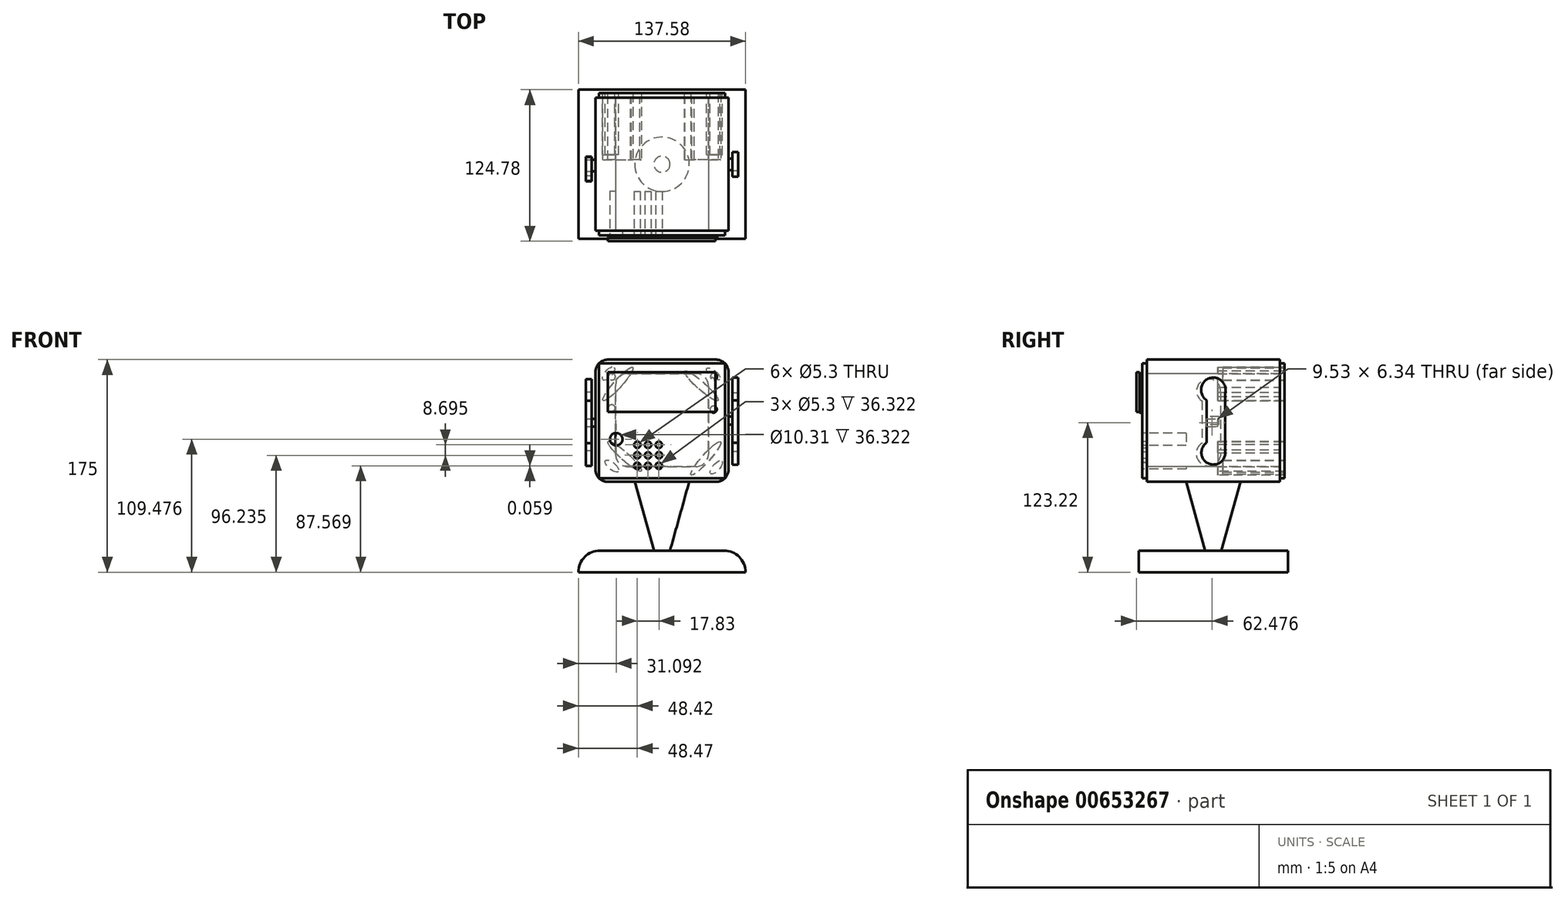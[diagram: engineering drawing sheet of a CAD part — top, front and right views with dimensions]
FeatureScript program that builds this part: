
annotation { "Feature Type Name" : "Feature", "Feature Type Description" : "" }
export const myFeature = defineFeature(function(context is Context, id is Id, definition is map)
    precondition{}
    {
        {
            var Q0;
            Q0=qCreatedBy(makeId("Top.planeOp"),FACE);
            var sketch = newSketch(context, id + "F0", { "sketchPlane" : qUnion([Q0])});
            skCircle(sketch, "E0.cCircle", {"center": v(0, 0) * mm, "radius": 54.77 * mm, "construction": true});
            skLineSegment(sketch, "E0.0", {"start": v(54.77, -54.77) * mm, "end": v(-54.77, -54.77) * mm});
            skLineSegment(sketch, "E0.1", {"start": v(-54.77, -54.77) * mm, "end": v(-54.77, 54.77) * mm});
            skLineSegment(sketch, "E0.2", {"start": v(-54.77, 54.77) * mm, "end": v(54.77, 54.77) * mm});
            skLineSegment(sketch, "E0.3", {"start": v(54.77, 54.77) * mm, "end": v(54.77, -54.77) * mm});
            skPoint(sketch, "E0.0.midPoint", {"position": v(0, -54.77) * mm});
            skSolve(sketch);
        }
        {
            var Q0;
            Q0 = qSketchRegion(id + "F0", true);
            extrude(context, id + "F1", {"entities" : qUnion([Q0]), "depth" : 100.58 * mm, "offsetDistance" : 25.4 * mm});
        }
        {
            var Q0;
            Q0=makeQuery(id+"F1.opExtrude","CAP_EDGE",EDGE,{"disambiguationData":[OSD([sQuery(id+"F0.wireOp",EDGE,"E0.1")])],"isStart":false});
            var Q1;
            Q1=makeQuery(id+"F1.opExtrude","CAP_EDGE",EDGE,{"disambiguationData":[OSD([sQuery(id+"F0.wireOp",EDGE,"E0.3")])],"isStart":false});
            var Q2;
            Q2=makeQuery(id+"F1.opExtrude","CAP_EDGE",EDGE,{"disambiguationData":[OSD([sQuery(id+"F0.wireOp",EDGE,"E0.3")])],"isStart":true});
            var Q3;
            Q3=makeQuery(id+"F1.opExtrude","CAP_EDGE",EDGE,{"disambiguationData":[OSD([sQuery(id+"F0.wireOp",EDGE,"E0.1")])],"isStart":true});
            fillet(context, id + "F2", {"entities" : qUnion([Q0, Q1, Q2, Q3]), "radius" : 10.16 * mm, "tangentPropagation" : true, "allowEdgeOverflow" : false});
        }
        {
            var Q0;
            Q0=makeQuery(id+"F1.opExtrude","SWEPT_FACE",FACE,{"disambiguationData":[OSD([sQuery(id+"F0.wireOp",EDGE,"E0.0")])]});
            var sketch = newSketch(context, id + "F3", { "sketchPlane" : qUnion([Q0])});
            skPoint(sketch, "E1", {"position": v(0, 50.3) * mm});
            skPoint(sketch, "E1.positionSnap0", {"position": v(-54.77, 50.3) * mm});
            skSolve(sketch);
        }
        {
            var Q0;
            {var subQ0=sQuery(id+"F0.wireOp",EDGE,"E0.0");Q0=makeQuery(id+"F3.imprint","IMPRINT",FACE,{"disambiguationData":[TD([[makeQuery(id+"F3.imprint","IMPRINT",EDGE,{"derivedFrom":makeQuery(id+"F1.opExtrude","CAP_EDGE",EDGE,{"disambiguationData":[OSD([subQ0])],"isStart":true})}),-1.0]])]});}
            var sketch = newSketch(context, id + "F4", { "sketchPlane" : qUnion([Q0])});
            skLineSegment(sketch, "E2.0", {"start": v(38.27, 12.57) * mm, "end": v(-38.27, 12.57) * mm});
            skLineSegment(sketch, "E2.1", {"start": v(-38.27, 12.57) * mm, "end": v(-38.27, 89.12) * mm});
            skLineSegment(sketch, "E2.2", {"start": v(-38.27, 89.12) * mm, "end": v(38.27, 89.12) * mm});
            skLineSegment(sketch, "E2.3", {"start": v(38.27, 89.12) * mm, "end": v(38.27, 12.57) * mm});
            skPoint(sketch, "E2.0.midPoint", {"position": v(0, 12.57) * mm});
            skSolve(sketch);
        }
        {
            var Q0;
            Q0=makeQuery(id+"F4.imprint","IMPRINT",FACE,{"disambiguationData":[TD([[makeQuery(id+"F4.imprint","IMPRINT",EDGE,{"derivedFrom":sQuery(id+"F4.wireOp",EDGE,"E2.0")}),-1.0]])]});
            extrude(context, id + "F5", {"entities" : qUnion([Q0]), "operationType" : NewBodyOperationType.REMOVE, "oppositeDirection" : true, "depth" : 148.34 * mm, "offsetDistance" : 25.4 * mm});
        }
        {
            var Q0;
            Q0=makeQuery(id+"F5.boolean.opBoolean","COPY",EDGE,{"derivedFrom":makeQuery(id+"F5.opExtrude","SWEPT_EDGE",EDGE,{"disambiguationData":[OSD([sQuery(id+"F4.wireOp",EDGE,"E2.0"),sQuery(id+"F4.wireOp",EDGE,"E2.1")])]})});
            var Q1;
            Q1=makeQuery(id+"F5.boolean.opBoolean","COPY",EDGE,{"derivedFrom":makeQuery(id+"F5.opExtrude","SWEPT_EDGE",EDGE,{"disambiguationData":[OSD([sQuery(id+"F4.wireOp",EDGE,"E2.2"),sQuery(id+"F4.wireOp",EDGE,"E2.3")])]})});
            var Q2;
            Q2=makeQuery(id+"F5.boolean.opBoolean","COPY",EDGE,{"derivedFrom":makeQuery(id+"F5.opExtrude","SWEPT_EDGE",EDGE,{"disambiguationData":[OSD([sQuery(id+"F4.wireOp",EDGE,"E2.0"),sQuery(id+"F4.wireOp",EDGE,"E2.3")])]})});
            var Q3;
            Q3=makeQuery(id+"F5.boolean.opBoolean","COPY",EDGE,{"derivedFrom":makeQuery(id+"F5.opExtrude","SWEPT_EDGE",EDGE,{"disambiguationData":[OSD([sQuery(id+"F4.wireOp",EDGE,"E2.1"),sQuery(id+"F4.wireOp",EDGE,"E2.2")])]})});
            fillet(context, id + "F6", {"entities" : qUnion([Q0, Q1, Q2, Q3]), "radius" : 10.16 * mm, "tangentPropagation" : true, "allowEdgeOverflow" : false});
        }
        {
            var Q0;
            Q0=makeQuery(id+"F1.opExtrude","SWEPT_FACE",FACE,{"disambiguationData":[OSD([sQuery(id+"F0.wireOp",EDGE,"E0.0")])]});
            var sketch = newSketch(context, id + "F7", { "sketchPlane" : qUnion([Q0])});
            skLineSegment(sketch, "E3.bottom", {"start": v(-51.8, 97.6) * mm, "end": v(51.8, 97.6) * mm});
            skLineSegment(sketch, "E3.top", {"start": v(-51.8, 2.98) * mm, "end": v(51.8, 2.98) * mm});
            skLineSegment(sketch, "E3.left", {"start": v(-51.8, 97.6) * mm, "end": v(-51.8, 2.98) * mm});
            skLineSegment(sketch, "E3.right", {"start": v(51.8, 97.6) * mm, "end": v(51.8, 2.98) * mm});
            skSolve(sketch);
        }
        {
            var Q0;
            Q0 = qSketchRegion(id + "F7", true);
            extrude(context, id + "F8", {"entities" : qUnion([Q0]), "operationType" : NewBodyOperationType.ADD, "depth" : 3.8 * mm, "offsetDistance" : 25.4 * mm});
        }
        {
            var Q0;
            Q0=makeQuery(id+"F1.opExtrude","CAP_FACE",FACE,{"disambiguationData":[OSD([sQuery(id+"F0.wireOp",EDGE,"E0.0"),sQuery(id+"F0.wireOp",EDGE,"E0.1"),sQuery(id+"F0.wireOp",EDGE,"E0.2"),sQuery(id+"F0.wireOp",EDGE,"E0.3")])],"isStart":true});
            var sketch = newSketch(context, id + "F9", { "sketchPlane" : qUnion([Q0])});
            skCircle(sketch, "E4", {"center": v(0, 0) * mm, "radius": 22.39 * mm});
            skSolve(sketch);
        }
        {
            var Q0;
            Q0=qCreatedBy(makeId("Top.planeOp"),FACE);
            cPlane(context, id + "F10", {"entities" : qUnion([Q0]), "cplaneType" : CPlaneType.OFFSET, "offset" : 56.64 * mm, "oppositeDirection" : true, "width" : 152.4 * mm, "height" : 152.4 * mm});
        }
        {
            var Q0;
            Q0=qCreatedBy(id+"F10.planeOp",FACE);
            var sketch = newSketch(context, id + "F11", { "sketchPlane" : qUnion([Q0])});
            skCircle(sketch, "E5", {"center": v(0, 0) * mm, "radius": 6.62 * mm});
            skSolve(sketch);
        }
        {
            var Q1;
            Q1=makeQuery(id+"F9.imprint","IMPRINT",FACE,{"disambiguationData":[TD([[makeQuery(id+"F9.imprint","IMPRINT",EDGE,{"derivedFrom":sQuery(id+"F9.wireOp",EDGE,"E4")}),1.0]])]});
            var Q2;
            Q2=makeQuery(id+"F11.imprint","IMPRINT",FACE,{"disambiguationData":[TD([[makeQuery(id+"F11.imprint","IMPRINT",EDGE,{"derivedFrom":sQuery(id+"F11.wireOp",EDGE,"E5")}),1.0]])]});
            loft(context, id + "F12", {"operationType" : NewBodyOperationType.ADD, "sheetProfilesArray" : [{ "sheetProfileEntities" : qUnion([Q1]) }, { "sheetProfileEntities" : qUnion([Q2]) }]});
        }
        {
            var Q0;
            Q0=qCreatedBy(id+"F10.planeOp",FACE);
            cPlane(context, id + "F13", {"entities" : qUnion([Q0]), "cplaneType" : CPlaneType.OFFSET, "offset" : 17.78 * mm, "oppositeDirection" : true, "width" : 152.4 * mm, "height" : 152.4 * mm});
        }
        {
            var Q0;
            Q0=qCreatedBy(id+"F13.planeOp",FACE);
            var sketch = newSketch(context, id + "F14", { "sketchPlane" : qUnion([Q0])});
            skLineSegment(sketch, "E6.bottom", {"start": v(68.8, -61.37) * mm, "end": v(-68.8, -61.37) * mm});
            skLineSegment(sketch, "E6.top", {"start": v(68.8, 61.37) * mm, "end": v(-68.8, 61.37) * mm});
            skLineSegment(sketch, "E6.left", {"start": v(68.8, -61.37) * mm, "end": v(68.8, 61.37) * mm});
            skLineSegment(sketch, "E6.right", {"start": v(-68.8, -61.37) * mm, "end": v(-68.8, 61.37) * mm});
            skPoint(sketch, "E6.middle", {"position": v(0, 0) * mm});
            skSolve(sketch);
        }
        {
            var Q0;
            Q0=makeQuery(id+"F14.imprint","IMPRINT",FACE,{"disambiguationData":[TD([[makeQuery(id+"F14.imprint","IMPRINT",EDGE,{"derivedFrom":sQuery(id+"F14.wireOp",EDGE,"E6.bottom")}),-1.0]])]});
            extrude(context, id + "F15", {"entities" : qUnion([Q0]), "operationType" : NewBodyOperationType.ADD, "depth" : 17.78 * mm, "offsetDistance" : 25.4 * mm});
        }
        {
            var Q0;
            Q0=makeQuery(id+"F15.opExtrude","CAP_EDGE",EDGE,{"disambiguationData":[OSD([sQuery(id+"F14.wireOp",EDGE,"E6.left")])],"isStart":false});
            var Q1;
            Q1=makeQuery(id+"F15.opExtrude","CAP_EDGE",EDGE,{"disambiguationData":[OSD([sQuery(id+"F14.wireOp",EDGE,"E6.right")])],"isStart":false});
            fillet(context, id + "F16", {"entities" : qUnion([Q0, Q1]), "radius" : 17.78 * mm, "tangentPropagation" : true, "allowEdgeOverflow" : false});
        }
        {
            var Q0;
            Q0=makeQuery(id+"F1.opExtrude","SWEPT_FACE",FACE,{"disambiguationData":[OSD([sQuery(id+"F0.wireOp",EDGE,"E0.2")])]});
            var sketch = newSketch(context, id + "F17", { "sketchPlane" : qUnion([Q0])});
            skLineSegment(sketch, "E7.bottom", {"start": v(-51.8, 97.6) * mm, "end": v(51.8, 97.6) * mm});
            skLineSegment(sketch, "E7.top", {"start": v(-51.8, 2.98) * mm, "end": v(51.8, 2.98) * mm});
            skLineSegment(sketch, "E7.left", {"start": v(-51.8, 97.6) * mm, "end": v(-51.8, 2.98) * mm});
            skLineSegment(sketch, "E7.right", {"start": v(51.8, 97.6) * mm, "end": v(51.8, 2.98) * mm});
            skSolve(sketch);
        }
        {
            var Q0;
            Q0 = qSketchRegion(id + "F17", true);
            extrude(context, id + "F18", {"entities" : qUnion([Q0]), "operationType" : NewBodyOperationType.ADD, "depth" : 3.8 * mm, "offsetDistance" : 25.4 * mm});
        }
        {
            var Q0;
            Q0=makeQuery(id+"F18.opExtrude","CAP_FACE",FACE,{"disambiguationData":[OSD([sQuery(id+"F17.wireOp",EDGE,"E7.bottom"),sQuery(id+"F17.wireOp",EDGE,"E7.top"),sQuery(id+"F17.wireOp",EDGE,"E7.left"),sQuery(id+"F17.wireOp",EDGE,"E7.right")])],"isStart":false});
            var sketch = newSketch(context, id + "F19", { "sketchPlane" : qUnion([Q0])});
            skEllipse(sketch, "E8", {"center": v(-42.25, 88.86) * mm, "majorRadius": 6.99 * mm, "minorRadius": 2.87 * mm, "majorAxis": v(-0.76, -0.65)});
            skEllipse(sketch, "E9.1.0.0", {"center": v(41.15, 12.95) * mm, "majorRadius": 6.99 * mm, "minorRadius": 2.87 * mm, "majorAxis": v(-0.76, -0.65)});
            skEllipse(sketch, "E9.2.0.0", {"center": v(124.54, -62.95) * mm, "majorRadius": 6.99 * mm, "minorRadius": 2.87 * mm, "majorAxis": v(-0.76, -0.65)});
            skEllipse(sketch, "E10", {"center": v(44.02, 89.18) * mm, "majorRadius": 6.99 * mm, "minorRadius": 2.87 * mm, "majorAxis": v(-0.65, 0.76)});
            skEllipse(sketch, "E11.1.0.0", {"center": v(-44.7, 11.94) * mm, "majorRadius": 6.99 * mm, "minorRadius": 2.87 * mm, "majorAxis": v(-0.65, 0.76)});
            skSolve(sketch);
        }
        {
            var Q0;
            Q0=makeQuery(id+"F19.imprint","IMPRINT",FACE,{"disambiguationData":[TD([[makeQuery(id+"F19.imprint","IMPRINT",EDGE,{"derivedFrom":sQuery(id+"F19.wireOp",EDGE,"E8")}),1.0]])]});
            var Q1;
            Q1=makeQuery(id+"F19.imprint","IMPRINT",FACE,{"disambiguationData":[TD([[makeQuery(id+"F19.imprint","IMPRINT",EDGE,{"derivedFrom":sQuery(id+"F19.wireOp",EDGE,"E10")}),1.0]])]});
            var Q2;
            Q2=makeQuery(id+"F19.imprint","IMPRINT",FACE,{"disambiguationData":[TD([[makeQuery(id+"F19.imprint","IMPRINT",EDGE,{"derivedFrom":sQuery(id+"F19.wireOp",EDGE,"E9.1.0.0")}),1.0]])]});
            var Q3;
            Q3=makeQuery(id+"F19.imprint","IMPRINT",FACE,{"disambiguationData":[TD([[makeQuery(id+"F19.imprint","IMPRINT",EDGE,{"derivedFrom":sQuery(id+"F19.wireOp",EDGE,"E11.1.0.0")}),1.0]])]});
            extrude(context, id + "F20", {"entities" : qUnion([Q0, Q1, Q2, Q3]), "operationType" : NewBodyOperationType.REMOVE, "oppositeDirection" : true, "depth" : 50.8 * mm, "offsetDistance" : 25.4 * mm});
        }
        {
            var Q0;
            Q0=makeQuery(id+"F18.opExtrude","CAP_FACE",FACE,{"disambiguationData":[OSD([sQuery(id+"F17.wireOp",EDGE,"E7.bottom"),sQuery(id+"F17.wireOp",EDGE,"E7.top"),sQuery(id+"F17.wireOp",EDGE,"E7.left"),sQuery(id+"F17.wireOp",EDGE,"E7.right")])],"isStart":false});
            var sketch = newSketch(context, id + "F21", { "sketchPlane" : qUnion([Q0])});
            skEllipse(sketch, "E12", {"center": v(-32.4, 79) * mm, "majorRadius": 18.25 * mm, "minorRadius": 3.26 * mm, "majorAxis": v(-0.75, -0.66)});
            skEllipse(sketch, "E13.1.0.0", {"center": v(30.73, 21.08) * mm, "majorRadius": 18.25 * mm, "minorRadius": 3.26 * mm, "majorAxis": v(-0.75, -0.66)});
            skEllipse(sketch, "E14", {"center": v(36.25, 80.6) * mm, "majorRadius": 18.25 * mm, "minorRadius": 3.26 * mm, "majorAxis": v(-0.66, 0.75)});
            skEllipse(sketch, "E15.1.0.0", {"center": v(-36.07, 19.3) * mm, "majorRadius": 18.25 * mm, "minorRadius": 3.26 * mm, "majorAxis": v(-0.66, 0.75)});
            skSolve(sketch);
        }
        {
            var Q0;
            Q0=makeQuery(id+"F21.imprint","IMPRINT",FACE,{"disambiguationData":[TD([[makeQuery(id+"F21.imprint","IMPRINT",EDGE,{"derivedFrom":sQuery(id+"F21.wireOp",EDGE,"E12")}),1.0]])]});
            var Q1;
            Q1=makeQuery(id+"F21.imprint","IMPRINT",FACE,{"disambiguationData":[TD([[makeQuery(id+"F21.imprint","IMPRINT",EDGE,{"derivedFrom":sQuery(id+"F21.wireOp",EDGE,"E13.1.0.0")}),1.0]])]});
            var Q2;
            Q2=makeQuery(id+"F21.imprint","IMPRINT",FACE,{"disambiguationData":[TD([[makeQuery(id+"F21.imprint","IMPRINT",EDGE,{"derivedFrom":sQuery(id+"F21.wireOp",EDGE,"E15.1.0.0")}),1.0]])]});
            var Q3;
            Q3=makeQuery(id+"F21.imprint","IMPRINT",FACE,{"disambiguationData":[TD([[makeQuery(id+"F21.imprint","IMPRINT",EDGE,{"derivedFrom":sQuery(id+"F21.wireOp",EDGE,"E14")}),1.0]])]});
            extrude(context, id + "F22", {"entities" : qUnion([Q0, Q1, Q2, Q3]), "operationType" : NewBodyOperationType.REMOVE, "oppositeDirection" : true, "depth" : 54.86 * mm, "offsetDistance" : 25.4 * mm});
        }
        {
            var Q0;
            Q0=makeQuery(id+"F8.opExtrude","CAP_FACE",FACE,{"disambiguationData":[OSD([sQuery(id+"F7.wireOp",EDGE,"E3.bottom"),sQuery(id+"F7.wireOp",EDGE,"E3.top"),sQuery(id+"F7.wireOp",EDGE,"E3.left"),sQuery(id+"F7.wireOp",EDGE,"E3.right")])],"isStart":false});
            var sketch = newSketch(context, id + "F23", { "sketchPlane" : qUnion([Q0])});
            skCircle(sketch, "E16", {"center": v(-41.1, 86.58) * mm, "radius": 2.76 * mm});
            skCircle(sketch, "E17.1.0.0", {"center": v(42.67, 86.61) * mm, "radius": 2.76 * mm});
            skCircle(sketch, "E18.1.0.0", {"center": v(-41.4, 60.7) * mm, "radius": 2.76 * mm});
            skCircle(sketch, "E19.1.0.0", {"center": v(42.42, 59.7) * mm, "radius": 2.76 * mm});
            skSolve(sketch);
        }
        {
            var Q0;
            Q0=makeQuery(id+"F23.imprint","IMPRINT",FACE,{"disambiguationData":[TD([[makeQuery(id+"F23.imprint","IMPRINT",EDGE,{"derivedFrom":sQuery(id+"F23.wireOp",EDGE,"E17.2.0.0")}),1.0]])]});
            var Q1;
            Q1=makeQuery(id+"F23.imprint","IMPRINT",FACE,{"disambiguationData":[TD([[makeQuery(id+"F23.imprint","IMPRINT",EDGE,{"derivedFrom":sQuery(id+"F23.wireOp",EDGE,"E16")}),1.0]])]});
            var Q2;
            Q2=makeQuery(id+"F23.imprint","IMPRINT",FACE,{"disambiguationData":[TD([[makeQuery(id+"F23.imprint","IMPRINT",EDGE,{"derivedFrom":sQuery(id+"F23.wireOp",EDGE,"E18.1.0.0")}),1.0]])]});
            var Q3;
            Q3=makeQuery(id+"F23.imprint","IMPRINT",FACE,{"disambiguationData":[TD([[makeQuery(id+"F23.imprint","IMPRINT",EDGE,{"derivedFrom":sQuery(id+"F23.wireOp",EDGE,"E17.1.0.0")}),1.0]])]});
            var Q4;
            Q4=makeQuery(id+"F23.imprint","IMPRINT",FACE,{"disambiguationData":[TD([[makeQuery(id+"F23.imprint","IMPRINT",EDGE,{"derivedFrom":sQuery(id+"F23.wireOp",EDGE,"E19.1.0.0")}),1.0]])]});
            extrude(context, id + "F24", {"entities" : qUnion([Q0, Q1, Q2, Q3, Q4]), "operationType" : NewBodyOperationType.ADD, "depth" : 2.03 * mm, "offsetDistance" : 25.4 * mm});
        }
        {
            var Q0;
            Q0=makeQuery(id+"F24.opExtrude","CAP_FACE",FACE,{"disambiguationData":[OSD([sQuery(id+"F23.wireOp",EDGE,"E19.1.0.0")])],"isStart":false});
            var sketch = newSketch(context, id + "F25", { "sketchPlane" : qUnion([Q0])});
            skLineSegment(sketch, "E20.bottom", {"start": v(-44.52, 90.37) * mm, "end": v(43.99, 90.37) * mm});
            skLineSegment(sketch, "E20.top", {"start": v(-44.52, 57.42) * mm, "end": v(43.99, 57.42) * mm});
            skLineSegment(sketch, "E20.left", {"start": v(-44.52, 90.37) * mm, "end": v(-44.52, 57.42) * mm});
            skLineSegment(sketch, "E20.right", {"start": v(43.99, 90.37) * mm, "end": v(43.99, 57.42) * mm});
            skSolve(sketch);
        }
        {
            var Q0;
            Q0 = qSketchRegion(id + "F25", true);
            extrude(context, id + "F26", {"entities" : qUnion([Q0]), "operationType" : NewBodyOperationType.ADD, "depth" : 2.8 * mm, "offsetDistance" : 25.4 * mm});
        }
        {
            var Q0;
            Q0=makeQuery(id+"F8.opExtrude","CAP_FACE",FACE,{"disambiguationData":[OSD([sQuery(id+"F7.wireOp",EDGE,"E3.bottom"),sQuery(id+"F7.wireOp",EDGE,"E3.top"),sQuery(id+"F7.wireOp",EDGE,"E3.left"),sQuery(id+"F7.wireOp",EDGE,"E3.right")])],"isStart":false});
            var sketch = newSketch(context, id + "F27", { "sketchPlane" : qUnion([Q0])});
            skCircle(sketch, "E21", {"center": v(-37.7, 35.06) * mm, "radius": 5.15 * mm});
            skCircle(sketch, "E22", {"center": v(-20.27, 30.5) * mm, "radius": 2.65 * mm});
            skCircle(sketch, "E23.1.0.0", {"center": v(-11.43, 30.48) * mm, "radius": 2.65 * mm});
            skCircle(sketch, "E23.2.0.0", {"center": v(-2.59, 30.45) * mm, "radius": 2.65 * mm});
            skCircle(sketch, "E24.1.0.0", {"center": v(-20.32, 21.84) * mm, "radius": 2.65 * mm});
            skCircle(sketch, "E24.1.0.1", {"center": v(-11.48, 21.81) * mm, "radius": 2.65 * mm});
            skCircle(sketch, "E24.2.0.0", {"center": v(-20.37, 13.18) * mm, "radius": 2.65 * mm});
            skCircle(sketch, "E24.2.0.1", {"center": v(-11.53, 13.15) * mm, "radius": 2.65 * mm});
            skCircle(sketch, "E25.1.0.0", {"center": v(-2.54, 13.2) * mm, "radius": 2.65 * mm});
            skCircle(sketch, "E25.1.0.1", {"center": v(-2.5, 21.87) * mm, "radius": 2.65 * mm});
            skSolve(sketch);
        }
        {
            var Q0;
            Q0=makeQuery(id+"F27.imprint","IMPRINT",FACE,{"disambiguationData":[TD([[makeQuery(id+"F27.imprint","IMPRINT",EDGE,{"derivedFrom":sQuery(id+"F27.wireOp",EDGE,"E21")}),1.0]])]});
            var Q1;
            Q1=makeQuery(id+"F27.imprint","IMPRINT",FACE,{"disambiguationData":[TD([[makeQuery(id+"F27.imprint","IMPRINT",EDGE,{"derivedFrom":sQuery(id+"F27.wireOp",EDGE,"E22")}),1.0]])]});
            var Q2;
            Q2=makeQuery(id+"F27.imprint","IMPRINT",FACE,{"disambiguationData":[TD([[makeQuery(id+"F27.imprint","IMPRINT",EDGE,{"derivedFrom":sQuery(id+"F27.wireOp",EDGE,"E23.1.0.0")}),1.0]])]});
            var Q3;
            Q3=makeQuery(id+"F27.imprint","IMPRINT",FACE,{"disambiguationData":[TD([[makeQuery(id+"F27.imprint","IMPRINT",EDGE,{"derivedFrom":sQuery(id+"F27.wireOp",EDGE,"E23.2.0.0")}),1.0]])]});
            var Q4;
            Q4=makeQuery(id+"F27.imprint","IMPRINT",FACE,{"disambiguationData":[TD([[makeQuery(id+"F27.imprint","IMPRINT",EDGE,{"derivedFrom":sQuery(id+"F27.wireOp",EDGE,"E25.1.0.1")}),1.0]])]});
            var Q5;
            Q5=makeQuery(id+"F27.imprint","IMPRINT",FACE,{"disambiguationData":[TD([[makeQuery(id+"F27.imprint","IMPRINT",EDGE,{"derivedFrom":sQuery(id+"F27.wireOp",EDGE,"E24.1.0.1")}),1.0]])]});
            var Q6;
            Q6=makeQuery(id+"F27.imprint","IMPRINT",FACE,{"disambiguationData":[TD([[makeQuery(id+"F27.imprint","IMPRINT",EDGE,{"derivedFrom":sQuery(id+"F27.wireOp",EDGE,"E24.1.0.0")}),1.0]])]});
            var Q7;
            Q7=makeQuery(id+"F27.imprint","IMPRINT",FACE,{"disambiguationData":[TD([[makeQuery(id+"F27.imprint","IMPRINT",EDGE,{"derivedFrom":sQuery(id+"F27.wireOp",EDGE,"E24.2.0.0")}),1.0]])]});
            var Q8;
            Q8=makeQuery(id+"F27.imprint","IMPRINT",FACE,{"disambiguationData":[TD([[makeQuery(id+"F27.imprint","IMPRINT",EDGE,{"derivedFrom":sQuery(id+"F27.wireOp",EDGE,"E24.2.0.1")}),1.0]])]});
            var Q9;
            Q9=makeQuery(id+"F27.imprint","IMPRINT",FACE,{"disambiguationData":[TD([[makeQuery(id+"F27.imprint","IMPRINT",EDGE,{"derivedFrom":sQuery(id+"F27.wireOp",EDGE,"E25.1.0.0")}),1.0]])]});
            var Q10;
            Q10=sQuery(id+"F27.wireOp",EDGE,"E21");
            extrude(context, id + "F28", {"entities" : qUnion([Q0, Q1, Q2, Q3, Q4, Q5, Q6, Q7, Q8, Q9]), "operationType" : NewBodyOperationType.REMOVE, "surfaceEntities" : qUnion([Q10]), "oppositeDirection" : true, "depth" : 36.32 * mm, "offsetDistance" : 25.4 * mm});
        }
        {
            var Q0;
            Q0=makeQuery(id+"F1.opExtrude","SWEPT_FACE",FACE,{"disambiguationData":[OSD([sQuery(id+"F0.wireOp",EDGE,"E0.3")])]});
            var sketch = newSketch(context, id + "F29", { "sketchPlane" : qUnion([Q0])});
            skLineSegment(sketch, "E26.bottom", {"start": v(4.77, 46.96) * mm, "end": v(-4.77, 46.96) * mm});
            skLineSegment(sketch, "E26.top", {"start": v(4.77, 53.63) * mm, "end": v(-4.77, 53.63) * mm});
            skLineSegment(sketch, "E26.left", {"start": v(4.77, 46.96) * mm, "end": v(4.77, 53.63) * mm});
            skLineSegment(sketch, "E26.right", {"start": v(-4.77, 46.96) * mm, "end": v(-4.77, 53.63) * mm});
            skPoint(sketch, "E26.middle", {"position": v(0, 50.3) * mm});
            skPoint(sketch, "E26.middle.positionSnap0", {"position": v(0, 10.16) * mm});
            skPoint(sketch, "E26.middle.positionSnap1", {"position": v(-54.77, 50.3) * mm});
            skPoint(sketch, "E26.centerSnap0", {"position": v(0, 10.16) * mm});
            skPoint(sketch, "E26.centerSnap1", {"position": v(-54.77, 50.3) * mm});
            skSolve(sketch);
        }
        {
            var Q0;
            Q0 = qSketchRegion(id + "F29", true);
            extrude(context, id + "F30", {"entities" : qUnion([Q0]), "operationType" : NewBodyOperationType.ADD, "depth" : 3.05 * mm, "offsetDistance" : 25.4 * mm});
        }
        {
            var Q0;
            Q0=makeQuery(id+"F30.opExtrude","CAP_FACE",FACE,{"disambiguationData":[OSD([sQuery(id+"F29.wireOp",EDGE,"E26.bottom"),sQuery(id+"F29.wireOp",EDGE,"E26.top"),sQuery(id+"F29.wireOp",EDGE,"E26.left"),sQuery(id+"F29.wireOp",EDGE,"E26.right")])],"isStart":false});
            var sketch = newSketch(context, id + "F31", { "sketchPlane" : qUnion([Q0])});
            skCircle(sketch, "E27", {"center": v(0, 75.69) * mm, "radius": 10.1 * mm});
            skPoint(sketch, "E27.centerSnap0", {"position": v(0, 53.63) * mm});
            skCircle(sketch, "E28", {"center": v(0, 24.03) * mm, "radius": 9.84 * mm});
            skPoint(sketch, "E28.centerSnap0", {"position": v(0, 46.96) * mm});
            skLineSegment(sketch, "E29", {"start": v(9.81, 24.74) * mm, "end": v(9.81, 73.25) * mm});
            skLineSegment(sketch, "E30", {"start": v(-5.45, 32.22) * mm, "end": v(-5.45, 67.17) * mm});
            skSolve(sketch);
        }
        {
            var Q0;
            Q0 = qSketchRegion(id + "F31", true);
            extrude(context, id + "F32", {"entities" : qUnion([Q0]), "depth" : 4.83 * mm, "offsetDistance" : 25.4 * mm});
        }
        {
            var Q0;
            Q0=makeQuery(id+"F1.opExtrude","SWEPT_FACE",FACE,{"disambiguationData":[OSD([sQuery(id+"F0.wireOp",EDGE,"E0.1")])]});
            var sketch = newSketch(context, id + "F33", { "sketchPlane" : qUnion([Q0])});
            skLineSegment(sketch, "E31.bottom", {"start": v(5.7, 45.63) * mm, "end": v(-3.83, 45.63) * mm});
            skLineSegment(sketch, "E31.top", {"start": v(5.7, 51.97) * mm, "end": v(-3.83, 51.97) * mm});
            skLineSegment(sketch, "E31.left", {"start": v(5.7, 45.63) * mm, "end": v(5.7, 51.97) * mm});
            skLineSegment(sketch, "E31.right", {"start": v(-3.83, 45.63) * mm, "end": v(-3.83, 51.97) * mm});
            skSolve(sketch);
        }
        {
            var Q0;
            Q0 = qSketchRegion(id + "F33", true);
            extrude(context, id + "F34", {"entities" : qUnion([Q0]), "operationType" : NewBodyOperationType.ADD, "depth" : 3.05 * mm, "offsetDistance" : 25.4 * mm});
        }
        {
            var Q0;
            Q0=makeQuery(id+"F34.opExtrude","CAP_FACE",FACE,{"disambiguationData":[OSD([sQuery(id+"F33.wireOp",EDGE,"E31.bottom"),sQuery(id+"F33.wireOp",EDGE,"E31.top"),sQuery(id+"F33.wireOp",EDGE,"E31.left"),sQuery(id+"F33.wireOp",EDGE,"E31.right")])],"isStart":false});
            var sketch = newSketch(context, id + "F35", { "sketchPlane" : qUnion([Q0])});
            skCircle(sketch, "E32.2.0", {"center": v(3.91, 23.18) * mm, "radius": 10.1 * mm});
            skLineSegment(sketch, "E32.2.1", {"start": v(-5.9, 74.16) * mm, "end": v(-5.9, 25.65) * mm});
            skLineSegment(sketch, "E32.2.2", {"start": v(9.36, 66.67) * mm, "end": v(9.36, 31.7) * mm});
            skCircle(sketch, "E32.2.3", {"center": v(3.92, 74.86) * mm, "radius": 9.84 * mm});
            skSolve(sketch);
        }
        {
            var Q0;
            {var subQ1=sQuery(id+"F35.wireOp",EDGE,"E32.2.1");Q0=makeQuery(id+"F35.imprint","IMPRINT",FACE,{"disambiguationData":[TD([[makeQuery(id+"F35.imprint","IMPRINT",EDGE,{"derivedFrom":subQ1}),1.0]])]});}
            var Q1;
            {var subQ0=sQuery(id+"F35.wireOp",EDGE,"E32.2.3");var subQ1=makeQuery(id+"F35.imprint","INTERSECT",VERTEX,{"derivedFrom":[sQuery(id+"F35.wireOp",EDGE,"E32.2.1"),subQ0]});Q1=makeQuery(id+"F35.imprint","IMPRINT",FACE,{"disambiguationData":[TD([[makeQuery(id+"F35.imprint","IMPRINT",EDGE,{"disambiguationData":[TD([[subQ1,-1.0]])],"derivedFrom":subQ0}),1.0]])]});}
            var Q2;
            {var subQ0=sQuery(id+"F35.wireOp",EDGE,"E32.2.0");var subQ1=makeQuery(id+"F35.imprint","INTERSECT",VERTEX,{"derivedFrom":[subQ0,sQuery(id+"F35.wireOp",EDGE,"E32.2.1")]});Q2=makeQuery(id+"F35.imprint","IMPRINT",FACE,{"disambiguationData":[TD([[makeQuery(id+"F35.imprint","IMPRINT",EDGE,{"disambiguationData":[TD([[subQ1,1.0]])],"derivedFrom":subQ0}),1.0]])]});}
            var Q3;
            Q3=sQuery(id+"F35.wireOp",EDGE,"E32.2.3");
            var Q4;
            Q4=sQuery(id+"F35.wireOp",EDGE,"E32.2.0");
            var Q5;
            Q5=sQuery(id+"F35.wireOp",EDGE,"E32.2.2");
            extrude(context, id + "F36", {"entities" : qUnion([Q0, Q1, Q2]), "surfaceEntities" : qUnion([Q3, Q4, Q5]), "depth" : 4.83 * mm, "offsetDistance" : 25.4 * mm});
        }
    });
